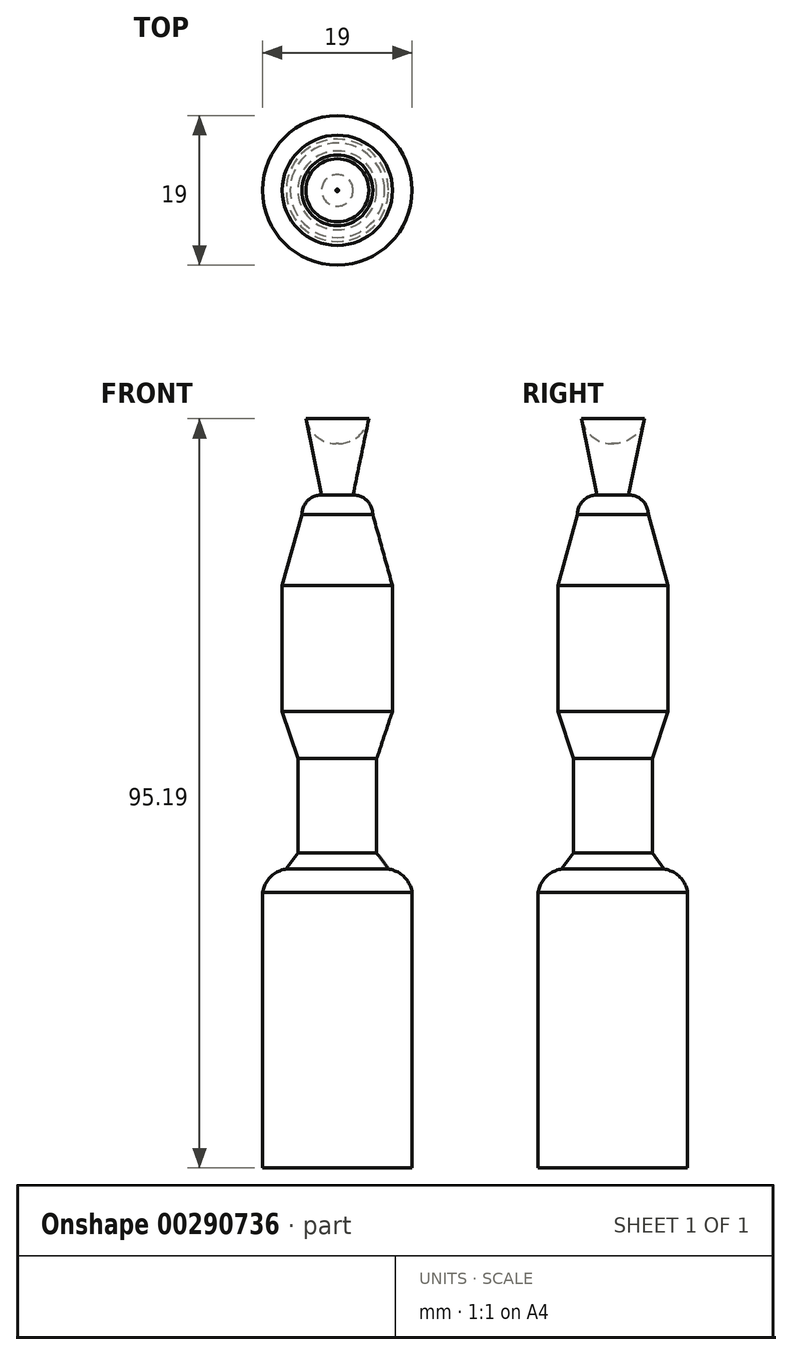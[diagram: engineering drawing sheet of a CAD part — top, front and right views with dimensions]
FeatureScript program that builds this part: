
annotation { "Feature Type Name" : "Feature", "Feature Type Description" : "" }
export const myFeature = defineFeature(function(context is Context, id is Id, definition is map)
    precondition{}
    {
        {
            var Q0;
            Q0=qCreatedBy(makeId("Front.planeOp"),FACE);
            var sketch = newSketch(context, id + "F0", { "sketchPlane" : qUnion([Q0])});
            skLineSegment(sketch, "E0", {"start": v(4, -4.8) * mm, "end": v(2, -14.5) * mm});
            skArc(sketch, "E1", {"start": v(4.5, -17) * mm, "mid": v(3.77, -15.23) * mm, "end": v(2, -14.5) * mm});
            skLineSegment(sketch, "E2", {"start": v(4.5, -17) * mm, "end": v(7, -26) * mm});
            skLineSegment(sketch, "E3", {"start": v(7, -26) * mm, "end": v(7, -42) * mm});
            skLineSegment(sketch, "E4", {"start": v(7, -42) * mm, "end": v(5, -48) * mm});
            skLineSegment(sketch, "E5", {"start": v(5, -48) * mm, "end": v(5, -60) * mm});
            skLineSegment(sketch, "E6", {"start": v(5, -60) * mm, "end": v(6.5, -62) * mm});
            skLineSegment(sketch, "E7", {"start": v(6, -62) * mm, "end": v(6.5, -62) * mm});
            skArc(sketch, "E8", {"start": v(9.5, -65) * mm, "mid": v(8.3, -62.85) * mm, "end": v(6, -62) * mm});
            skLineSegment(sketch, "E9", {"start": v(9.5, -100) * mm, "end": v(9.5, -65) * mm});
            skLineSegment(sketch, "E10", {"start": v(0, -100) * mm, "end": v(9.5, -100) * mm});
            skLineSegment(sketch, "E11", {"start": v(0, 0) * mm, "end": v(0, -100) * mm});
            skArc(sketch, "E12", {"start": v(4, -4.8) * mm, "mid": v(3.16, -1.44) * mm, "end": v(0, 0) * mm});
            skSolve(sketch);
        }
        {
            var Q0;
            Q0 = qSketchRegion(id + "F0", true);
            var Q1;
            Q1=sQuery(id+"F0.wireOp",EDGE,"E11");
            revolve(context, id + "F1", {"entities" : qUnion([Q0]), "axis" : qUnion([Q1]), "revolveType" : RevolveType.FULL});
        }
    });
